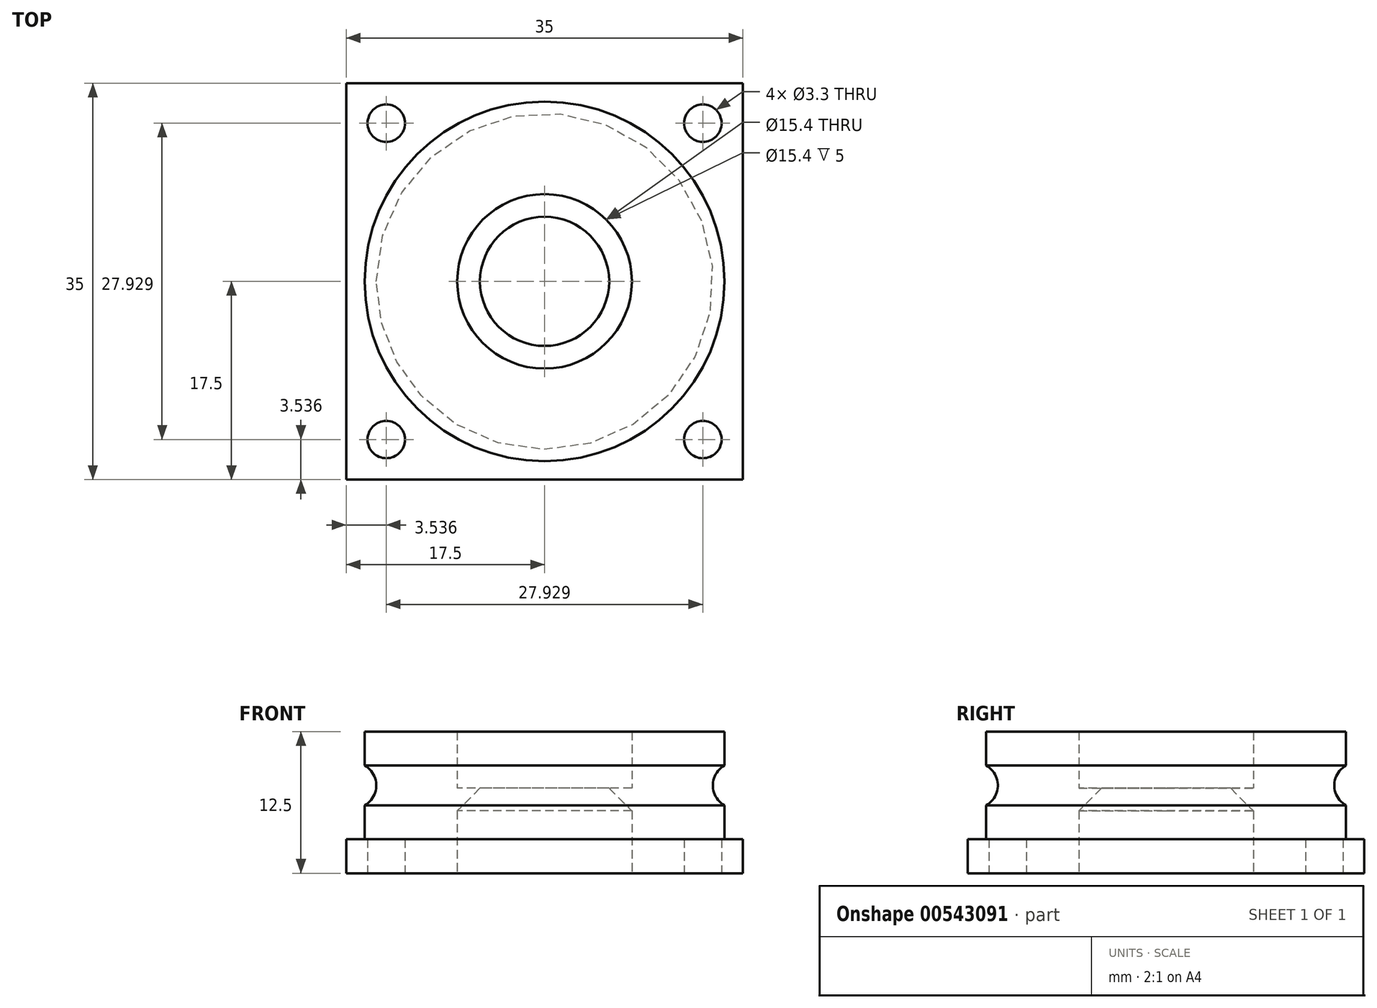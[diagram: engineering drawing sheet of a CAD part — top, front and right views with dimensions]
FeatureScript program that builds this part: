
annotation { "Feature Type Name" : "Feature", "Feature Type Description" : "" }
export const myFeature = defineFeature(function(context is Context, id is Id, definition is map)
    precondition{}
    {
        {
            assignVariable(context, id + "F0", {"name" : "PulleyThickness", "anyValue" : 9.5 * mm});
        }
        {
            assignVariable(context, id + "F1", {"name" : "BaseThickness", "anyValue" : 3 * mm});
        }
        {
            var Q0;
            Q0=qCreatedBy(makeId("Top.planeOp"),FACE);
            var sketch = newSketch(context, id + "F2", { "sketchPlane" : qUnion([Q0])});
            skLineSegment(sketch, "E0.bottom", {"start": v(-17.5, 17.5) * mm, "end": v(17.5, 17.5) * mm});
            skLineSegment(sketch, "E0.top", {"start": v(-17.5, -17.5) * mm, "end": v(17.5, -17.5) * mm});
            skLineSegment(sketch, "E0.left", {"start": v(-17.5, 17.5) * mm, "end": v(-17.5, -17.5) * mm});
            skLineSegment(sketch, "E0.right", {"start": v(17.5, 17.5) * mm, "end": v(17.5, -17.5) * mm});
            skCircle(sketch, "E1", {"center": v(0, 0) * mm, "radius": 15.88 * mm});
            skLineSegment(sketch, "E2", {"start": v(-17.5, 17.5) * mm, "end": v(-13.96, 13.96) * mm, "construction": true});
            skLineSegment(sketch, "E3", {"start": v(17.5, 17.5) * mm, "end": v(13.96, 13.96) * mm, "construction": true});
            skLineSegment(sketch, "E4.trimOffspring", {"start": v(11.23, -11.23) * mm, "end": v(13.96, -13.96) * mm, "construction": true});
            skLineSegment(sketch, "E5.trimOffspring", {"start": v(-11.23, -11.23) * mm, "end": v(-13.96, -13.96) * mm, "construction": true});
            skLineSegment(sketch, "E6", {"start": v(-13.96, 13.96) * mm, "end": v(-11.23, 11.23) * mm, "construction": true});
            skLineSegment(sketch, "E7", {"start": v(13.96, 13.96) * mm, "end": v(11.23, 11.23) * mm, "construction": true});
            skLineSegment(sketch, "E8", {"start": v(13.96, -13.96) * mm, "end": v(17.5, -17.5) * mm, "construction": true});
            skLineSegment(sketch, "E9", {"start": v(-13.96, -13.96) * mm, "end": v(-17.5, -17.5) * mm, "construction": true});
            skCircle(sketch, "E10", {"center": v(0, 0) * mm, "radius": 7.7 * mm});
            skSolve(sketch);
        }
        {
            var Q0;
            Q0=makeQuery(id+"F2.imprint","IMPRINT",FACE,{"disambiguationData":[TD([[makeQuery(id+"F2.imprint","IMPRINT",EDGE,{"derivedFrom":sQuery(id+"F2.wireOp",EDGE,"E0.bottom")}),-1.0]])]});
            var Q1;
            Q1=makeQuery(id+"F2.imprint","IMPRINT",FACE,{"disambiguationData":[TD([[makeQuery(id+"F2.imprint","IMPRINT",EDGE,{"derivedFrom":sQuery(id+"F2.wireOp",EDGE,"E1")}),1.0]])]});
            extrude(context, id + "F3", {"entities" : qUnion([Q0, Q1]), "depth" : getVariable(context, 'BaseThickness'), "offsetDistance" : 25 * mm});
        }
        {
            var Q0;
            Q0=sQuery(id+"F2.wireOp",VERTEX,"E9.start");
            var Q1;
            Q1=sQuery(id+"F2.wireOp",VERTEX,"E2.end");
            var Q2;
            Q2=sQuery(id+"F2.wireOp",VERTEX,"E3.end");
            var Q3;
            Q3=sQuery(id+"F2.wireOp",VERTEX,"E8.start");
            var Q4;
            Q4=makeQuery(id+"F3.opExtrude","SWEPT_BODY",BODY,{"disambiguationData":[OSD([sQuery(id+"F2.wireOp",EDGE,"E0.bottom"),sQuery(id+"F2.wireOp",EDGE,"E0.top"),sQuery(id+"F2.wireOp",EDGE,"E0.left"),sQuery(id+"F2.wireOp",EDGE,"E0.right"),sQuery(id+"F2.wireOp",EDGE,"E10")])]});
            hole(context, id + "F4", {"style" : HoleStyle.SIMPLE, "endStyle" : HoleEndStyle.BLIND, "oppositeDirection" : true, "standardTappedOrClearance" : lookupTablePath({ "standard" : "ISO", "fit" : "Normal", "size" : "M3", "type" : "Clearance" }), "standardBlindInLast" : lookupTablePath({ "fit" : "Standard", "standard" : "ISO", "size" : "M3", "type" : "Clearance" }), "holeDiameter" : 3.3 * mm, "holeDepth" : 13.9 * mm, "isTappedThrough" : true, "tappedDepth" : 12 * mm, "tapClearance" : 3, "locations" : qUnion([Q0, Q1, Q2, Q3]), "scope" : qUnion([Q4])});
        }
        {
            var Q0;
            Q0=makeQuery(id+"F3.opExtrude","CAP_FACE",FACE,{"disambiguationData":[OSD([sQuery(id+"F2.wireOp",EDGE,"E0.bottom"),sQuery(id+"F2.wireOp",EDGE,"E0.top"),sQuery(id+"F2.wireOp",EDGE,"E0.left"),sQuery(id+"F2.wireOp",EDGE,"E0.right"),sQuery(id+"F2.wireOp",EDGE,"E10")])],"isStart":false});
            var sketch = newSketch(context, id + "F5", { "sketchPlane" : qUnion([Q0])});
            skCircle(sketch, "E11.0", {"center": v(0, 0) * mm, "radius": 15.88 * mm});
            skCircle(sketch, "E12.0", {"center": v(0, 0) * mm, "radius": 7.7 * mm});
            skSolve(sketch);
        }
        {
            var Q0;
            Q0 = qSketchRegion(id + "F5", true);
            extrude(context, id + "F6", {"entities" : qUnion([Q0]), "operationType" : NewBodyOperationType.ADD, "depth" : getVariable(context, 'PulleyThickness'), "offsetDistance" : 25 * mm});
        }
        {
            var Q0;
            Q0=qCreatedBy(makeId("Right.planeOp"),FACE);
            var sketch = newSketch(context, id + "F7", { "sketchPlane" : qUnion([Q0])});
            skLineSegment(sketch, "E13.0", {"start": v(-15.88, 12.5) * mm, "end": v(15.88, 12.5) * mm, "construction": true});
            skLineSegment(sketch, "E14", {"start": v(-15.88, 3) * mm, "end": v(0, 3) * mm, "construction": true});
            skLineSegment(sketch, "E15", {"start": v(-15.88, 12.5) * mm, "end": v(-15.88, 9.5) * mm});
            skLineSegment(sketch, "E16", {"start": v(-15.88, 9.5) * mm, "end": v(-15.88, 6) * mm});
            skLineSegment(sketch, "E17", {"start": v(-15.88, 6) * mm, "end": v(-15.88, 3) * mm});
            skArc(sketch, "E18", {"start": v(-15.88, 6) * mm, "mid": v(-14.84, 7.75) * mm, "end": v(-15.88, 9.5) * mm});
            skLineSegment(sketch, "E19.0", {"start": v(17.5, 3) * mm, "end": v(-17.5, 3) * mm});
            skSolve(sketch);
        }
        {
            var Q0;
            Q0 = qSketchRegion(id + "F7", true);
            var Q1;
            Q1=makeQuery(id+"F6.opExtrude","SWEPT_FACE",FACE,{"disambiguationData":[OSD([sQuery(id+"F5.wireOp",EDGE,"E11.0")])]});
            revolve(context, id + "F8", {"operationType" : NewBodyOperationType.REMOVE, "entities" : qUnion([Q0]), "axis" : qUnion([Q1]), "revolveType" : RevolveType.FULL, "oppositeDirection" : true});
        }
        {
            var Q0;
            Q0=makeQuery(id+"F2.imprint","IMPRINT",FACE,{"disambiguationData":[TD([[makeQuery(id+"F2.imprint","IMPRINT",EDGE,{"derivedFrom":sQuery(id+"F2.wireOp",EDGE,"E10")}),1.0]])]});
            cPlane(context, id + "F9", {"entities" : qUnion([Q0]), "cplaneType" : CPlaneType.OFFSET, "offset" : 5.5 * mm, "width" : 150 * mm, "height" : 150 * mm});
        }
        {
            var Q0;
            Q0=qCreatedBy(id+"F9.planeOp",FACE);
            var sketch = newSketch(context, id + "F10", { "sketchPlane" : qUnion([Q0])});
            skCircle(sketch, "E20.0", {"center": v(0, 0) * mm, "radius": 7.7 * mm});
            skCircle(sketch, "E21", {"center": v(0, 0) * mm, "radius": 5.7 * mm});
            skSolve(sketch);
        }
        {
            var Q0;
            Q0 = qSketchRegion(id + "F10", true);
            extrude(context, id + "F11", {"entities" : qUnion([Q0]), "operationType" : NewBodyOperationType.ADD, "depth" : 2 * mm, "offsetDistance" : 25 * mm});
        }
        {
            var Q0;
            Q0=makeQuery(id+"F11.opExtrude","CAP_EDGE",EDGE,{"disambiguationData":[OSD([sQuery(id+"F10.wireOp",EDGE,"E21")])],"isStart":true});
            chamfer(context, id + "F12", {"entities" : qUnion([Q0]), "width" : 2 * mm, "tangentPropagation" : true});
        }
    });
